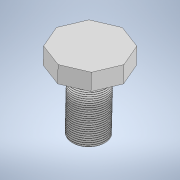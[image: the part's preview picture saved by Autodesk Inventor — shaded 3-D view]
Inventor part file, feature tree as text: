
AUTODESK INVENTOR PART (.ipt)
format: ipt  version: 2021 (Build 250183000, 183)  size: 1,212,416 bytes
history: native  units: in
note: dims shown in document units (in); Inventor stores cm internally (conversion verified against a paired STEP export)
features: other x4, sketch x4, extrude x3, plane x2, chamfer x1, helix x1
ambient origin geometry x8: Origin, YZ Plane, XZ Plane, XY Plane, X Axis, Y Axis, Z Axis, Center Point
bodies: Solid1 (feature_tree)
feature tree (15):
  plane  "Work Plane3"
  extrude  "Extrusion1"  Depth=2.126in TaperAngle=0.0deg
  extrude  "Extrusion2"  Depth=0.5906in TaperAngle=0.0deg
  chamfer  "Chamfer1"  Distance=0.0394in Angle=45.0deg
  other  "Work Axis1"
  extrude  "Extrusion3"  Depth=0.5906in TaperAngle=360.0deg
  plane  "Work Plane5"
  helix  "Coil2"  [1 undecoded]
  sketch  "Sketch3"  dims[d0=1.1811in d1=2.126in d2=0.0in]
  sketch  "Sketch4"  dims[d3=2.3622in d4=0.5906in d5=0.0in d8=0.0394in d9=0.0787in d10=45.0deg]
  sketch  "Sketch7"  dims[d27=45.0deg d28=3.1496in d30=360.0deg d32=0.5906in d33=0.0in]
  sketch  "Sketch8"  dims[d34=90.0deg d35=0.0787in d36=0.0295in d37=0.0079in d38=0.1181in d39=0.0669in d40=2.2343in d41=0.3937in d42=0.0in d43=90.0deg d44=90.0deg d45=0.0in d46=0.0in]
  parser-record x1  (decoder bookkeeping rows leaked as tree rows — omitted from the tree; the rows remain in map.json)
  other  "Pen_Plotter.iam"
  other  "Clamp_Main_Body:1"
note: 1 required parameter value undecoded (feature->parameter linkage not recoverable at this tier; creation-order binding heuristic only, values carry confidence <= 0.55)
note: 1 file-system path scrubbed to <path> (originals preserved in map.json)
